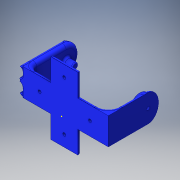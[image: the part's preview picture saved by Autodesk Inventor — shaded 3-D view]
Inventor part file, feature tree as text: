
AUTODESK INVENTOR PART (.ipt)
format: ipt  version: 2016 (Build 200138000, 138)  size: 572,928 bytes
history: native  units: in
note: dims shown in document units (in); Inventor stores cm internally (conversion verified against a paired STEP export)
features: sketch x12, other x3
ambient origin geometry x8: Origin, YZ Plane, XZ Plane, XY Plane, X Axis, Y Axis, Z Axis, Center Point
bodies: Solid1 (feature_tree)
feature tree (15):
  other  "Ankle.ipt"
  other  "Solid1::Ankle.ipt"
  other  "TaggingFeature1"
  sketch  "Sketch1"  dims[d0=0.3937in]
  sketch  "Sketch4"
  sketch  "Sketch5"
  sketch  "Sketch7"
  sketch  "Sketch9"
  sketch  "Sketch10"
  sketch  "Sketch15"
  sketch  "Sketch16"
  sketch  "Sketch17"
  sketch  "Sketch18"
  sketch  "Sketch19"
  sketch  "Sketch20"
